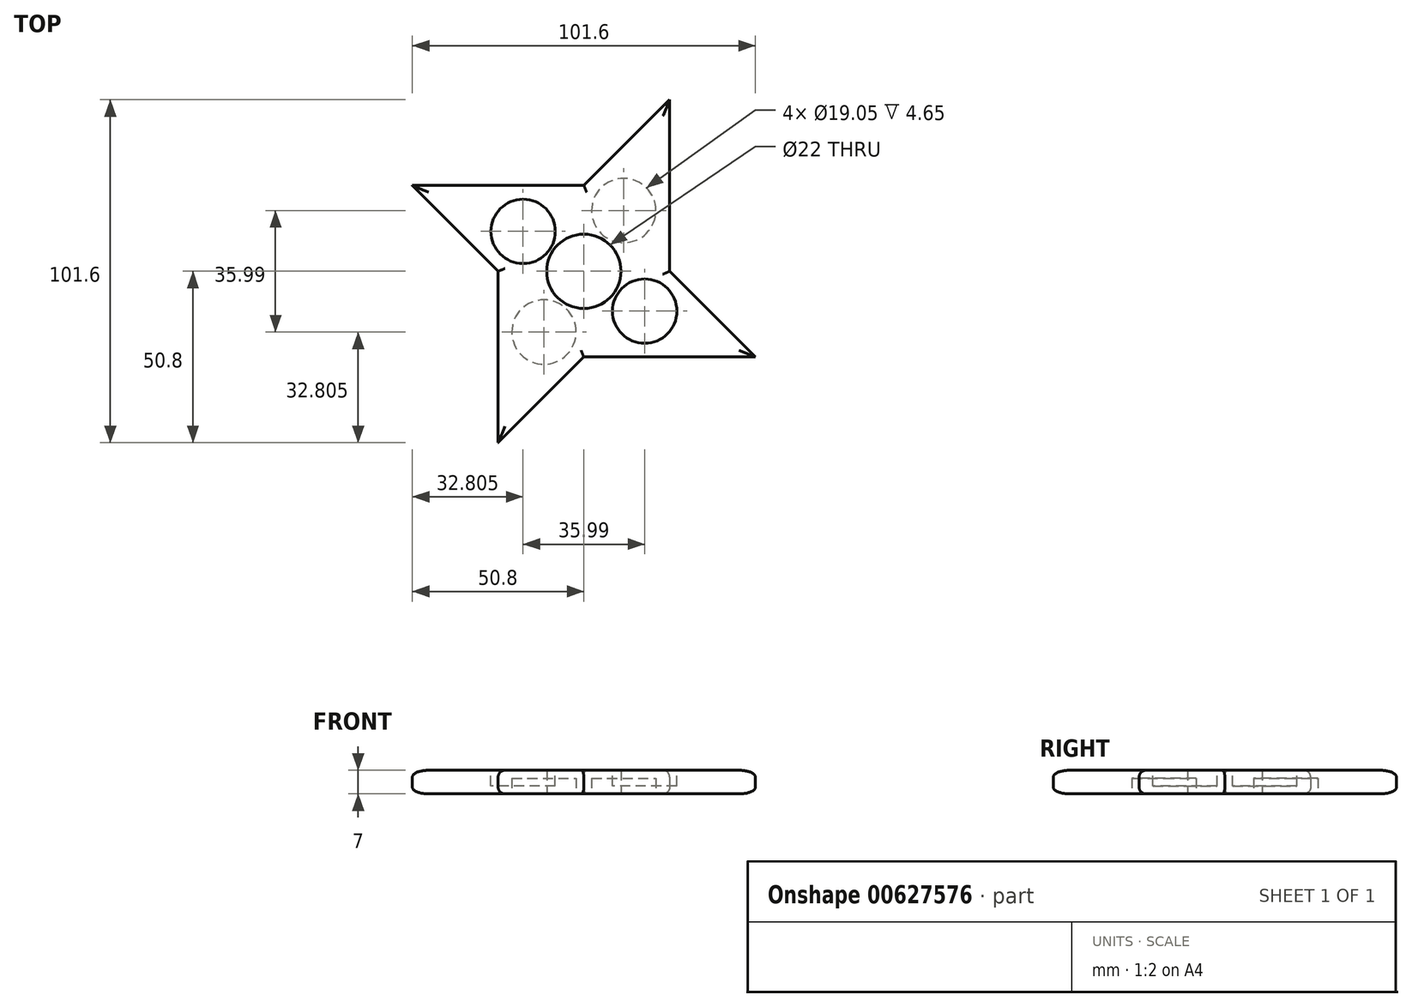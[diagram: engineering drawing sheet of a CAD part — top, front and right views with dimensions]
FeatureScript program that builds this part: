
annotation { "Feature Type Name" : "Feature", "Feature Type Description" : "" }
export const myFeature = defineFeature(function(context is Context, id is Id, definition is map)
    precondition{}
    {
        {
            var Q0;
            Q0=qCreatedBy(makeId("Top.planeOp"),FACE);
            var sketch = newSketch(context, id + "F0", { "sketchPlane" : qUnion([Q0])});
            skLineSegment(sketch, "E0.bottom", {"start": v(25.4, 25.4) * mm, "end": v(-25.4, 25.4) * mm});
            skLineSegment(sketch, "E0.top", {"start": v(25.4, -25.4) * mm, "end": v(-25.4, -25.4) * mm});
            skLineSegment(sketch, "E0.left", {"start": v(25.4, 25.4) * mm, "end": v(25.4, -25.4) * mm});
            skLineSegment(sketch, "E0.right", {"start": v(-25.4, 25.4) * mm, "end": v(-25.4, -25.4) * mm});
            skPoint(sketch, "E0.middle", {"position": v(0, 0) * mm});
            skCircle(sketch, "E1", {"center": v(0, 0) * mm, "radius": 11 * mm});
            skLineSegment(sketch, "E2", {"start": v(-25.4, 25.4) * mm, "end": v(-50.8, 25.4) * mm});
            skLineSegment(sketch, "E3", {"start": v(-50.8, 25.4) * mm, "end": v(-25.4, 0) * mm});
            skLineSegment(sketch, "E4", {"start": v(-25.4, -25.4) * mm, "end": v(-25.4, -50.8) * mm});
            skLineSegment(sketch, "E5", {"start": v(-25.4, -50.8) * mm, "end": v(0, -25.4) * mm});
            skLineSegment(sketch, "E6", {"start": v(25.4, -25.4) * mm, "end": v(50.8, -25.4) * mm});
            skLineSegment(sketch, "E7", {"start": v(50.8, -25.4) * mm, "end": v(25.4, 0) * mm});
            skLineSegment(sketch, "E8", {"start": v(25.4, 25.4) * mm, "end": v(25.4, 50.8) * mm});
            skLineSegment(sketch, "E9", {"start": v(25.4, 50.8) * mm, "end": v(0, 25.4) * mm});
            skSolve(sketch);
        }
        {
            var Q0;
            {var subQ0=sQuery(id+"F0.wireOp",EDGE,"E4");Q0=makeQuery(id+"F0.imprint","IMPRINT",FACE,{"disambiguationData":[TD([[makeQuery(id+"F0.imprint","IMPRINT",EDGE,{"derivedFrom":subQ0}),1.0]])]});}
            var Q1;
            Q1=makeQuery(id+"F0.imprint","IMPRINT",FACE,{"disambiguationData":[TD([[makeQuery(id+"F0.imprint","IMPRINT",EDGE,{"derivedFrom":sQuery(id+"F0.wireOp",EDGE,"E1")}),-1.0]])]});
            var Q2;
            Q2 = qSketchRegion(id + "F0", true);
            var Q3;
            {var subQ0=sQuery(id+"F0.wireOp",EDGE,"E2");Q3=makeQuery(id+"F0.imprint","IMPRINT",FACE,{"disambiguationData":[TD([[makeQuery(id+"F0.imprint","IMPRINT",EDGE,{"derivedFrom":subQ0}),1.0]])]});}
            var Q4;
            {var subQ0=sQuery(id+"F0.wireOp",EDGE,"E8");Q4=makeQuery(id+"F0.imprint","IMPRINT",FACE,{"disambiguationData":[TD([[makeQuery(id+"F0.imprint","IMPRINT",EDGE,{"derivedFrom":subQ0}),1.0]])]});}
            var Q5;
            {var subQ0=sQuery(id+"F0.wireOp",EDGE,"E6");Q5=makeQuery(id+"F0.imprint","IMPRINT",FACE,{"disambiguationData":[TD([[makeQuery(id+"F0.imprint","IMPRINT",EDGE,{"derivedFrom":subQ0}),1.0]])]});}
            extrude(context, id + "F1", {"entities" : qUnion([Q0, Q1, Q2, Q3, Q4, Q5]), "depth" : 7 * mm, "offsetDistance" : 25 * mm});
        }
        {
            var Q0;
            Q0=makeQuery(id+"F1.opExtrude","CAP_EDGE",EDGE,{"disambiguationData":[OSD([sQuery(id+"F0.wireOp",EDGE,"E0.bottom"),sQuery(id+"F0.wireOp",EDGE,"E2")])],"isStart":false});
            var Q1;
            Q1=makeQuery(id+"F1.opExtrude","CAP_EDGE",EDGE,{"disambiguationData":[OSD([sQuery(id+"F0.wireOp",EDGE,"E9")])],"isStart":false});
            var Q2;
            Q2=makeQuery(id+"F1.opExtrude","CAP_EDGE",EDGE,{"disambiguationData":[OSD([sQuery(id+"F0.wireOp",EDGE,"E3")])],"isStart":false});
            var Q3;
            Q3=makeQuery(id+"F1.opExtrude","CAP_EDGE",EDGE,{"disambiguationData":[OSD([sQuery(id+"F0.wireOp",EDGE,"E0.right"),sQuery(id+"F0.wireOp",EDGE,"E4")])],"isStart":false});
            var Q4;
            Q4=makeQuery(id+"F1.opExtrude","CAP_EDGE",EDGE,{"disambiguationData":[OSD([sQuery(id+"F0.wireOp",EDGE,"E5")])],"isStart":false});
            var Q5;
            Q5=makeQuery(id+"F1.opExtrude","CAP_EDGE",EDGE,{"disambiguationData":[OSD([sQuery(id+"F0.wireOp",EDGE,"E0.top"),sQuery(id+"F0.wireOp",EDGE,"E6")])],"isStart":false});
            var Q6;
            Q6=makeQuery(id+"F1.opExtrude","CAP_EDGE",EDGE,{"disambiguationData":[OSD([sQuery(id+"F0.wireOp",EDGE,"E7")])],"isStart":false});
            var Q7;
            Q7=makeQuery(id+"F1.opExtrude","CAP_EDGE",EDGE,{"disambiguationData":[OSD([sQuery(id+"F0.wireOp",EDGE,"E0.left"),sQuery(id+"F0.wireOp",EDGE,"E8")])],"isStart":false});
            var Q8;
            Q8=makeQuery(id+"F1.opExtrude","CAP_EDGE",EDGE,{"disambiguationData":[OSD([sQuery(id+"F0.wireOp",EDGE,"E0.bottom"),sQuery(id+"F0.wireOp",EDGE,"E2")])],"isStart":true});
            var Q9;
            Q9=makeQuery(id+"F1.opExtrude","CAP_EDGE",EDGE,{"disambiguationData":[OSD([sQuery(id+"F0.wireOp",EDGE,"E9")])],"isStart":true});
            var Q10;
            Q10=makeQuery(id+"F1.opExtrude","CAP_EDGE",EDGE,{"disambiguationData":[OSD([sQuery(id+"F0.wireOp",EDGE,"E0.left"),sQuery(id+"F0.wireOp",EDGE,"E8")])],"isStart":true});
            var Q11;
            Q11=makeQuery(id+"F1.opExtrude","CAP_EDGE",EDGE,{"disambiguationData":[OSD([sQuery(id+"F0.wireOp",EDGE,"E7")])],"isStart":true});
            var Q12;
            Q12=makeQuery(id+"F1.opExtrude","CAP_EDGE",EDGE,{"disambiguationData":[OSD([sQuery(id+"F0.wireOp",EDGE,"E0.top"),sQuery(id+"F0.wireOp",EDGE,"E6")])],"isStart":true});
            var Q13;
            Q13=makeQuery(id+"F1.opExtrude","CAP_EDGE",EDGE,{"disambiguationData":[OSD([sQuery(id+"F0.wireOp",EDGE,"E5")])],"isStart":true});
            var Q14;
            Q14=makeQuery(id+"F1.opExtrude","CAP_EDGE",EDGE,{"disambiguationData":[OSD([sQuery(id+"F0.wireOp",EDGE,"E0.right"),sQuery(id+"F0.wireOp",EDGE,"E4")])],"isStart":true});
            var Q15;
            Q15=makeQuery(id+"F1.opExtrude","CAP_EDGE",EDGE,{"disambiguationData":[OSD([sQuery(id+"F0.wireOp",EDGE,"E3")])],"isStart":true});
            fillet(context, id + "F2", {"entities" : qUnion([Q0, Q1, Q2, Q3, Q4, Q5, Q6, Q7, Q8, Q9, Q10, Q11, Q12, Q13, Q14, Q15]), "radius" : 2 * mm, "tangentPropagation" : true, "allowEdgeOverflow" : false});
        }
        {
            var Q0;
            Q0=makeQuery(id+"F1.opExtrude","CAP_FACE",FACE,{"disambiguationData":[OSD([sQuery(id+"F0.wireOp",EDGE,"E0.bottom"),sQuery(id+"F0.wireOp",EDGE,"E0.top"),sQuery(id+"F0.wireOp",EDGE,"E0.left"),sQuery(id+"F0.wireOp",EDGE,"E0.right"),sQuery(id+"F0.wireOp",EDGE,"E1"),sQuery(id+"F0.wireOp",EDGE,"E2"),sQuery(id+"F0.wireOp",EDGE,"E3"),sQuery(id+"F0.wireOp",EDGE,"E4"),sQuery(id+"F0.wireOp",EDGE,"E5"),sQuery(id+"F0.wireOp",EDGE,"E6"),sQuery(id+"F0.wireOp",EDGE,"E7"),sQuery(id+"F0.wireOp",EDGE,"E8"),sQuery(id+"F0.wireOp",EDGE,"E9")])],"isStart":false});
            var sketch = newSketch(context, id + "F3", { "sketchPlane" : qUnion([Q0])});
            skCircle(sketch, "E10", {"center": v(18, -11.81) * mm, "radius": 9.53 * mm});
            skSolve(sketch);
        }
        {
            var Q0;
            Q0 = qSketchRegion(id + "F3", true);
            var Q1;
            Q1=makeQuery(id+"F3.imprint","IMPRINT",FACE,{"disambiguationData":[TD([[makeQuery(id+"F3.imprint","IMPRINT",EDGE,{"derivedFrom":sQuery(id+"F3.wireOp",EDGE,"E10")}),1.0]])]});
            extrude(context, id + "F4", {"entities" : qUnion([Q0, Q1]), "operationType" : NewBodyOperationType.REMOVE, "oppositeDirection" : true, "depth" : 4.65 * mm, "offsetDistance" : 25 * mm});
        }
        {
            var Q0;
            Q0=makeQuery(id+"F1.opExtrude","CAP_FACE",FACE,{"disambiguationData":[OSD([sQuery(id+"F0.wireOp",EDGE,"E0.bottom"),sQuery(id+"F0.wireOp",EDGE,"E0.top"),sQuery(id+"F0.wireOp",EDGE,"E0.left"),sQuery(id+"F0.wireOp",EDGE,"E0.right"),sQuery(id+"F0.wireOp",EDGE,"E1"),sQuery(id+"F0.wireOp",EDGE,"E2"),sQuery(id+"F0.wireOp",EDGE,"E3"),sQuery(id+"F0.wireOp",EDGE,"E4"),sQuery(id+"F0.wireOp",EDGE,"E5"),sQuery(id+"F0.wireOp",EDGE,"E6"),sQuery(id+"F0.wireOp",EDGE,"E7"),sQuery(id+"F0.wireOp",EDGE,"E8"),sQuery(id+"F0.wireOp",EDGE,"E9")])],"isStart":false});
            var sketch = newSketch(context, id + "F5", { "sketchPlane" : qUnion([Q0])});
            skCircle(sketch, "E11", {"center": v(-18, 11.81) * mm, "radius": 9.53 * mm});
            skSolve(sketch);
        }
        {
            var Q0;
            Q0 = qSketchRegion(id + "F5", true);
            var Q1;
            Q1=makeQuery(id+"F5.imprint","IMPRINT",FACE,{"disambiguationData":[TD([[makeQuery(id+"F5.imprint","IMPRINT",EDGE,{"derivedFrom":sQuery(id+"F5.wireOp",EDGE,"E11")}),1.0]])]});
            extrude(context, id + "F6", {"entities" : qUnion([Q0, Q1]), "operationType" : NewBodyOperationType.REMOVE, "oppositeDirection" : true, "depth" : 4.65 * mm, "offsetDistance" : 25 * mm});
        }
        {
            var Q0;
            Q0=makeQuery(id+"F1.opExtrude","CAP_FACE",FACE,{"disambiguationData":[OSD([sQuery(id+"F0.wireOp",EDGE,"E0.bottom"),sQuery(id+"F0.wireOp",EDGE,"E0.top"),sQuery(id+"F0.wireOp",EDGE,"E0.left"),sQuery(id+"F0.wireOp",EDGE,"E0.right"),sQuery(id+"F0.wireOp",EDGE,"E1"),sQuery(id+"F0.wireOp",EDGE,"E2"),sQuery(id+"F0.wireOp",EDGE,"E3"),sQuery(id+"F0.wireOp",EDGE,"E4"),sQuery(id+"F0.wireOp",EDGE,"E5"),sQuery(id+"F0.wireOp",EDGE,"E6"),sQuery(id+"F0.wireOp",EDGE,"E7"),sQuery(id+"F0.wireOp",EDGE,"E8"),sQuery(id+"F0.wireOp",EDGE,"E9")])],"isStart":true});
            var sketch = newSketch(context, id + "F7", { "sketchPlane" : qUnion([Q0])});
            skCircle(sketch, "E12", {"center": v(-11.81, 18) * mm, "radius": 9.53 * mm});
            skSolve(sketch);
        }
        {
            var Q0;
            Q0=makeQuery(id+"F7.imprint","IMPRINT",FACE,{"disambiguationData":[TD([[makeQuery(id+"F7.imprint","IMPRINT",EDGE,{"derivedFrom":sQuery(id+"F7.wireOp",EDGE,"E12")}),1.0]])]});
            extrude(context, id + "F8", {"entities" : qUnion([Q0]), "operationType" : NewBodyOperationType.REMOVE, "oppositeDirection" : true, "depth" : 4.65 * mm, "offsetDistance" : 25 * mm});
        }
        {
            var Q0;
            Q0=makeQuery(id+"F1.opExtrude","CAP_FACE",FACE,{"disambiguationData":[OSD([sQuery(id+"F0.wireOp",EDGE,"E0.bottom"),sQuery(id+"F0.wireOp",EDGE,"E0.top"),sQuery(id+"F0.wireOp",EDGE,"E0.left"),sQuery(id+"F0.wireOp",EDGE,"E0.right"),sQuery(id+"F0.wireOp",EDGE,"E1"),sQuery(id+"F0.wireOp",EDGE,"E2"),sQuery(id+"F0.wireOp",EDGE,"E3"),sQuery(id+"F0.wireOp",EDGE,"E4"),sQuery(id+"F0.wireOp",EDGE,"E5"),sQuery(id+"F0.wireOp",EDGE,"E6"),sQuery(id+"F0.wireOp",EDGE,"E7"),sQuery(id+"F0.wireOp",EDGE,"E8"),sQuery(id+"F0.wireOp",EDGE,"E9")])],"isStart":true});
            var sketch = newSketch(context, id + "F9", { "sketchPlane" : qUnion([Q0])});
            skCircle(sketch, "E13", {"center": v(11.81, -18) * mm, "radius": 9.53 * mm});
            skSolve(sketch);
        }
        {
            var Q0;
            Q0=makeQuery(id+"F9.imprint","IMPRINT",FACE,{"disambiguationData":[TD([[makeQuery(id+"F9.imprint","IMPRINT",EDGE,{"derivedFrom":sQuery(id+"F9.wireOp",EDGE,"E13")}),1.0]])]});
            extrude(context, id + "F10", {"entities" : qUnion([Q0]), "operationType" : NewBodyOperationType.REMOVE, "oppositeDirection" : true, "depth" : 4.65 * mm, "offsetDistance" : 25 * mm});
        }
    });
